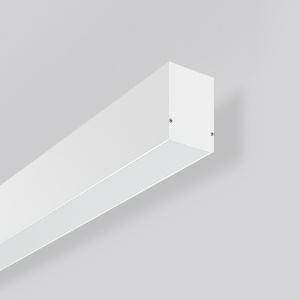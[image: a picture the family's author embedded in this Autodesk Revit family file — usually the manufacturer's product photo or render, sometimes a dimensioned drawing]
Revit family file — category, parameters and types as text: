
# Revit family: less_is_more_50_312614_002_76_d43e
name_source: partatom
category: Lighting Fixtures
units: mm (PartAtom-declared; Revit-internal decimal feet)

## family parameters
Cut with Voids When Loaded = No
Host = Face
Light Source = No
Part Type = Normal
Room Calculation Point = No
Round Connector Dimension = Use Diameter
Shared = No

## types (1)
- LESS IS MORE 50 (1 x LED Modul 830, 4550 lm, 3000)
    Apparent Load = 34 VA
    CIE Flux Codes = 48 80 96 50 100
    Color Rendering = 80
    Color Temperature = 3000
    Default Elevation = 1800 mm
    Description = Series: LESS IS MORE 50
Linear wall luminaires. Housing: extruded aluminium profile, powder-coated. End cap aluminium powder-coated. Diffuser made of non-yellowing plastic (PMMA), opal. Direct 50%, indirect 50% light emission. Suitable for Wall (surface). LED unit with integrated converter interchangeable and removable. Suitable for through-wiring. With sensors or as a safety luminaire on request. 
Colour: traffic white, matt (RAL 9016)
Length: 1967 mm
Width: 67 mm
Height: 75 mm
Lamp: LED
Socket: without socket
Colour temperature: 3000K
Colour rendering index (CRI): 80
Light source: LED
Socket lamp2: Without base
Colour temperature: 3000K
Colour rendering index (CRI) 2: 80
System power: 34 W
Rated luminous flux: 4550 lm
Luminous efficiency: 134 lm/W
Control gear: Converter, dimmable, DALI
Control gear: Converter, dimmable, DALI
Protection class: I
Type of protection: IP 20
    Height = 75 mm
    Lamp = 1 x LED Modul 830
    Lamp Light Flux = 4550 lm
    Lamp count = 1
    Length = 1967 mm
    Lifetime = 50000 h
    Luminous efficacy = 134 lm/W
    Manufacturer = RZB
    ModVariant = No
    Model = 312614.002.76
    Mounting Place = Wall
    Mounting Type = Surface mounted
    Number of Poles = 1
    OnlyDefault = Yes
    Power Factor = 1
    Product Name = LESS IS MORE 50
    Product group = Surface mounted LED linear luminaires
    ProductGroupID = 2007
    Protection Class = Protection class I
    Protection Degree = IP 20
    RLX_Detail_Level = 1
    RLX_Emergency_Light_Flux = 0 lm
    RLX_Emergency_Type = 0
    RLX_Emergency_Type_DB = No
    RlxData = <blob elided: 39645 chars, md5=859d5823>
    Socket = socket
    Standby Power = 0 W
    System Light Flux = 4550 lm
    System Power = 34 W
    Type Comments = Product without accessories
    Type Image = 312606.002.jpg
    URL = http://relux.com
    VarID = ---
    Voltage = 0 V
    Weight = 0.00 kg
    Width = 67 mm

## geometry (parser evidence)
native form markers: Blend x4, Sweep x11
no freeform markers — native parametric forms only
